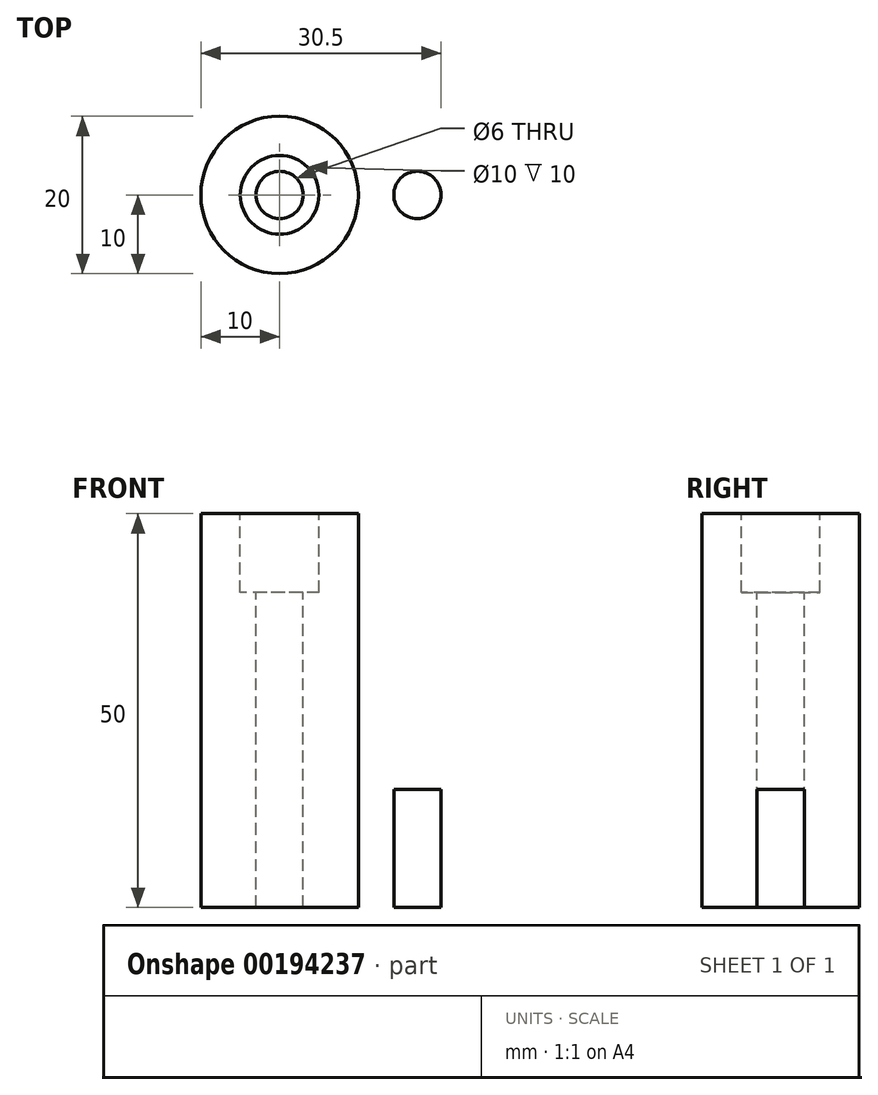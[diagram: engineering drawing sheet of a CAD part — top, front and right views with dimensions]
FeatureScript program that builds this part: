
annotation { "Feature Type Name" : "Feature", "Feature Type Description" : "" }
export const myFeature = defineFeature(function(context is Context, id is Id, definition is map)
    precondition{}
    {
        {
            var Q0;
            Q0=qCreatedBy(makeId("Top.planeOp"),FACE);
            var sketch = newSketch(context, id + "F0", { "sketchPlane" : qUnion([Q0])});
            skCircle(sketch, "E0", {"center": v(0, 0) * mm, "radius": 25 * mm});
            skSolve(sketch);
        }
        {
            var Q0;
            Q0=makeQuery(id+"F0.imprint","IMPRINT",FACE,{"disambiguationData":[TD([[makeQuery(id+"F0.imprint","IMPRINT",EDGE,{"derivedFrom":sQuery(id+"F0.wireOp",EDGE,"E0")}),1.0]])]});
            extrude(context, id + "F1", {"entities" : qUnion([Q0]), "depth" : 15 * mm});
        }
        {
            var Q0;
            Q0=makeQuery(id+"F1.opExtrude","CAP_FACE",FACE,{"disambiguationData":[OSD([sQuery(id+"F0.wireOp",EDGE,"E0")])],"isStart":false});
            var sketch = newSketch(context, id + "F2", { "sketchPlane" : qUnion([Q0])});
            skCircle(sketch, "E1", {"center": v(0, 0) * mm, "radius": 10 * mm});
            skSolve(sketch);
        }
        {
            var Q0;
            Q0 = qSketchRegion(id + "F2", true);
            extrude(context, id + "F3", {"entities" : qUnion([Q0]), "operationType" : NewBodyOperationType.ADD, "depth" : 35 * mm});
        }
        {
            var Q0;
            Q0=makeQuery(id+"F1.opExtrude","CAP_FACE",FACE,{"disambiguationData":[OSD([sQuery(id+"F0.wireOp",EDGE,"E0")])],"isStart":false});
            var sketch = newSketch(context, id + "F4", { "sketchPlane" : qUnion([Q0])});
            skCircle(sketch, "E2", {"center": v(-17.5, 0) * mm, "radius": 3 * mm});
            skCircle(sketch, "E3.MirrorC", {"center": v(17.5, 0) * mm, "radius": 3 * mm});
            skSolve(sketch);
        }
        {
            var Q0;
            Q0=makeQuery(id+"F4.imprint","IMPRINT",FACE,{"disambiguationData":[TD([[makeQuery(id+"F4.imprint","IMPRINT",EDGE,{"derivedFrom":sQuery(id+"F4.wireOp",EDGE,"E2")}),1.0]])]});
            var Q1;
            Q1=makeQuery(id+"F4.imprint","IMPRINT",FACE,{"disambiguationData":[TD([[makeQuery(id+"F4.imprint","IMPRINT",EDGE,{"derivedFrom":sQuery(id+"F4.wireOp",EDGE,"E3.MirrorC")}),-1.0]])]});
            extrude(context, id + "F5", {"entities" : qUnion([Q0, Q1]), "operationType" : NewBodyOperationType.REMOVE, "oppositeDirection" : true, "depth" : 15 * mm});
        }
        {
            var Q0;
            Q0=makeQuery(id+"F3.opExtrude","CAP_FACE",FACE,{"disambiguationData":[OSD([sQuery(id+"F2.wireOp",EDGE,"E1")])],"isStart":false});
            var sketch = newSketch(context, id + "F6", { "sketchPlane" : qUnion([Q0])});
            skCircle(sketch, "E4", {"center": v(0, 0) * mm, "radius": 3 * mm});
            skSolve(sketch);
        }
        {
            var Q0;
            Q0=makeQuery(id+"F6.imprint","IMPRINT",FACE,{"disambiguationData":[TD([[makeQuery(id+"F6.imprint","IMPRINT",EDGE,{"derivedFrom":sQuery(id+"F6.wireOp",EDGE,"E4")}),1.0]])]});
            var Q1;
            Q1=sQuery(id+"F6.wireOp",EDGE,"E4");
            extrude(context, id + "F7", {"entities" : qUnion([Q0]), "operationType" : NewBodyOperationType.REMOVE, "surfaceEntities" : qUnion([Q1]), "oppositeDirection" : true, "depth" : 50 * mm});
        }
        {
            var Q0;
            Q0=makeQuery(id+"F3.opExtrude","CAP_FACE",FACE,{"disambiguationData":[OSD([sQuery(id+"F2.wireOp",EDGE,"E1")])],"isStart":false});
            var sketch = newSketch(context, id + "F8", { "sketchPlane" : qUnion([Q0])});
            skCircle(sketch, "E5", {"center": v(0, 0) * mm, "radius": 5 * mm});
            skSolve(sketch);
        }
        {
            var Q0;
            Q0=makeQuery(id+"F8.imprint","IMPRINT",FACE,{"disambiguationData":[TD([[makeQuery(id+"F8.imprint","IMPRINT",EDGE,{"derivedFrom":sQuery(id+"F8.wireOp",EDGE,"E5")}),1.0]])]});
            var Q1;
            Q1=sQuery(id+"F8.wireOp",EDGE,"E5");
            extrude(context, id + "F9", {"entities" : qUnion([Q0]), "operationType" : NewBodyOperationType.REMOVE, "surfaceEntities" : qUnion([Q1]), "oppositeDirection" : true, "depth" : 10 * mm});
        }
    });
